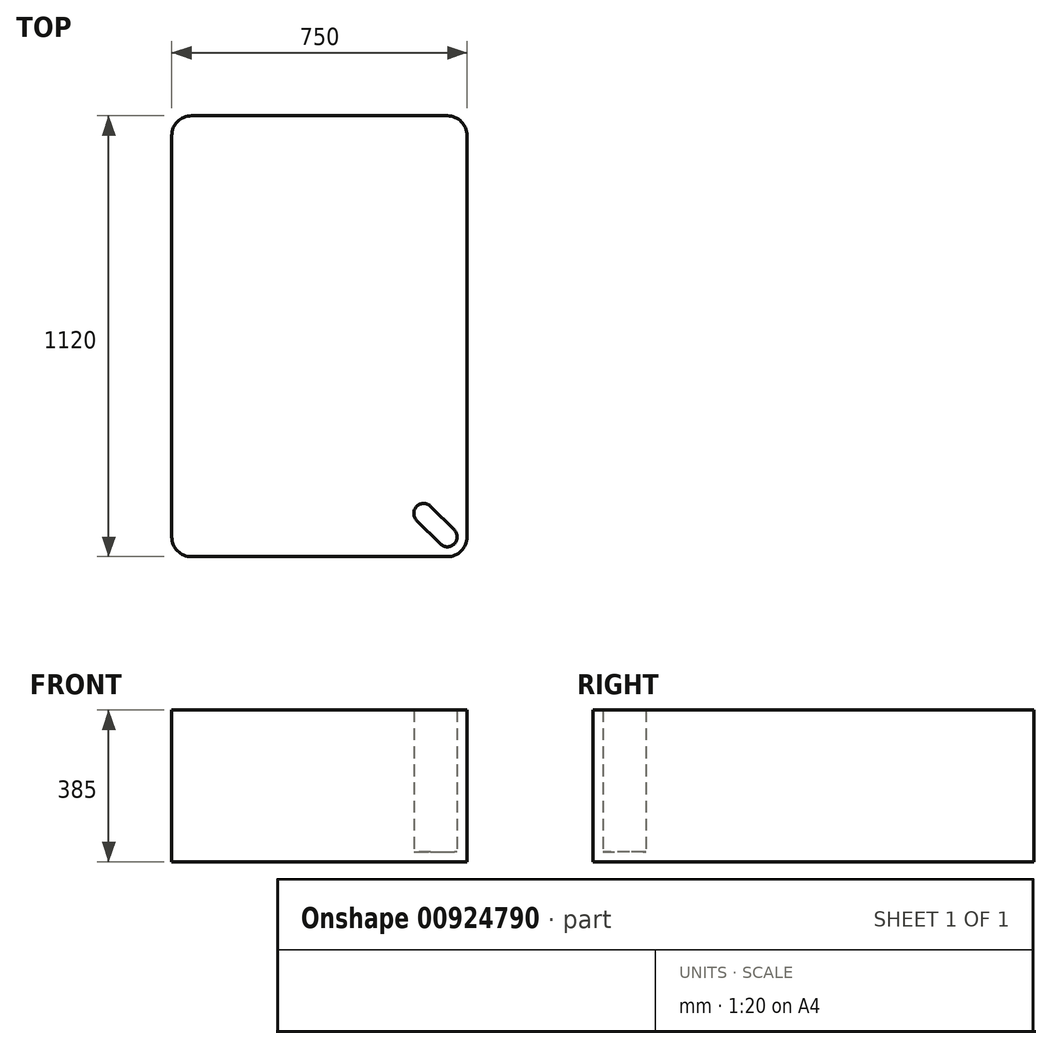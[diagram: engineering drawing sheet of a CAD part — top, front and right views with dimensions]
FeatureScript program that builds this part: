
annotation { "Feature Type Name" : "Feature", "Feature Type Description" : "" }
export const myFeature = defineFeature(function(context is Context, id is Id, definition is map)
    precondition{}
    {
        {
            var Q0;
            Q0=qCreatedBy(makeId("Top.planeOp"),FACE);
            var sketch = newSketch(context, id + "F0", { "sketchPlane" : qUnion([Q0])});
            skLineSegment(sketch, "E0.bottom", {"start": v(-325, 560) * mm, "end": v(325, 560) * mm});
            skLineSegment(sketch, "E0.top", {"start": v(-325, -560) * mm, "end": v(325, -560) * mm});
            skLineSegment(sketch, "E0.left", {"start": v(-375, 510) * mm, "end": v(-375, -510) * mm});
            skLineSegment(sketch, "E0.right", {"start": v(375, 510) * mm, "end": v(375, -510) * mm});
            skPoint(sketch, "E1.visualSharp", {"position": v(-375, 560) * mm});
            skArc(sketch, "E1.filletArc", {"start": v(-325, 560) * mm, "mid": v(-360.36, 545.36) * mm, "end": v(-375, 510) * mm});
            skPoint(sketch, "E2.visualSharp", {"position": v(375, 560) * mm});
            skArc(sketch, "E2.filletArc", {"start": v(375, 510) * mm, "mid": v(360.36, 545.36) * mm, "end": v(325, 560) * mm});
            skPoint(sketch, "E3.visualSharp", {"position": v(375, -560) * mm});
            skArc(sketch, "E3.filletArc", {"start": v(325, -560) * mm, "mid": v(360.36, -545.36) * mm, "end": v(375, -510) * mm});
            skPoint(sketch, "E4.visualSharp", {"position": v(-375, -560) * mm});
            skArc(sketch, "E4.filletArc", {"start": v(-375, -510) * mm, "mid": v(-360.36, -545.36) * mm, "end": v(-325, -560) * mm});
            skSolve(sketch);
        }
        {
            var Q0;
            Q0=makeQuery(id+"F0.imprint","IMPRINT",FACE,{"disambiguationData":[TD([[makeQuery(id+"F0.imprint","IMPRINT",EDGE,{"derivedFrom":sQuery(id+"F0.wireOp",EDGE,"E0.bottom")}),-1.0]])]});
            extrude(context, id + "F1", {"entities" : qUnion([Q0]), "depth" : 25 * mm, "offsetDistance" : 25 * mm});
        }
        {
            var Q0;
            Q0=makeQuery(id+"F1.opExtrude","CAP_FACE",FACE,{"disambiguationData":[OSD([sQuery(id+"F0.wireOp",EDGE,"E0.bottom"),sQuery(id+"F0.wireOp",EDGE,"E0.top"),sQuery(id+"F0.wireOp",EDGE,"E0.left"),sQuery(id+"F0.wireOp",EDGE,"E0.right"),sQuery(id+"F0.wireOp",EDGE,"E1.filletArc"),sQuery(id+"F0.wireOp",EDGE,"E2.filletArc"),sQuery(id+"F0.wireOp",EDGE,"E3.filletArc"),sQuery(id+"F0.wireOp",EDGE,"E4.filletArc")])],"isStart":false});
            var sketch = newSketch(context, id + "F2", { "sketchPlane" : qUnion([Q0])});
            skArc(sketch, "E5", {"start": v(-342.68, -492.32) * mm, "mid": v(-342.68, -527.68) * mm, "end": v(-307.32, -527.68) * mm});
            skArc(sketch, "E6", {"start": v(-247.32, -467.68) * mm, "mid": v(-247.32, -432.32) * mm, "end": v(-282.68, -432.32) * mm});
            skLineSegment(sketch, "E7", {"start": v(-282.68, -432.32) * mm, "end": v(-342.68, -492.32) * mm});
            skLineSegment(sketch, "E8", {"start": v(-247.32, -467.68) * mm, "end": v(-307.32, -527.68) * mm});
            skLineSegment(sketch, "E9.MirrorCS", {"start": v(282.68, -432.32) * mm, "end": v(342.68, -492.32) * mm});
            skArc(sketch, "E10.MirrorCS", {"start": v(342.68, -492.32) * mm, "mid": v(342.68, -527.68) * mm, "end": v(307.32, -527.68) * mm});
            skArc(sketch, "E11.MirrorCS", {"start": v(247.32, -467.68) * mm, "mid": v(247.32, -432.32) * mm, "end": v(282.68, -432.32) * mm});
            skLineSegment(sketch, "E12.MirrorCS", {"start": v(247.32, -467.68) * mm, "end": v(307.32, -527.68) * mm});
            skArc(sketch, "E13.MirrorCS", {"start": v(342.68, 492.32) * mm, "mid": v(342.68, 527.68) * mm, "end": v(307.32, 527.68) * mm});
            skLineSegment(sketch, "E14.MirrorCS", {"start": v(282.68, 432.32) * mm, "end": v(342.68, 492.32) * mm});
            skArc(sketch, "E15.MirrorCS", {"start": v(247.32, 467.68) * mm, "mid": v(247.32, 432.32) * mm, "end": v(282.68, 432.32) * mm});
            skLineSegment(sketch, "E16.MirrorCS", {"start": v(-247.32, 467.68) * mm, "end": v(-307.32, 527.68) * mm});
            skLineSegment(sketch, "E17.MirrorCS", {"start": v(247.32, 467.68) * mm, "end": v(307.32, 527.68) * mm});
            skArc(sketch, "E18.MirrorCS", {"start": v(-247.32, 467.68) * mm, "mid": v(-247.32, 432.32) * mm, "end": v(-282.68, 432.32) * mm});
            skLineSegment(sketch, "E19.MirrorCS", {"start": v(-282.68, 432.32) * mm, "end": v(-342.68, 492.32) * mm});
            skArc(sketch, "E20.MirrorCS", {"start": v(-342.68, 492.32) * mm, "mid": v(-342.68, 527.68) * mm, "end": v(-307.32, 527.68) * mm});
            skSolve(sketch);
        }
        {
            var Q0;
            Q0=makeQuery(id+"F2.imprint","IMPRINT",FACE,{"disambiguationData":[TD([[makeQuery(id+"F2.imprint","IMPRINT",EDGE,{"derivedFrom":sQuery(id+"F2.wireOp",EDGE,"E5")}),1.0]])]});
            var Q1;
            Q1=makeQuery(id+"F2.imprint","IMPRINT",FACE,{"disambiguationData":[TD([[makeQuery(id+"F2.imprint","IMPRINT",EDGE,{"derivedFrom":sQuery(id+"F2.wireOp",EDGE,"E10.MirrorCS")}),-1.0]])]});
            var Q2;
            Q2=makeQuery(id+"F2.imprint","IMPRINT",FACE,{"disambiguationData":[TD([[makeQuery(id+"F2.imprint","IMPRINT",EDGE,{"derivedFrom":sQuery(id+"F2.wireOp",EDGE,"E13.MirrorCS")}),1.0]])]});
            var Q3;
            Q3=makeQuery(id+"F2.imprint","IMPRINT",FACE,{"disambiguationData":[TD([[makeQuery(id+"F2.imprint","IMPRINT",EDGE,{"derivedFrom":sQuery(id+"F2.wireOp",EDGE,"E16.MirrorCS")}),1.0]])]});
            extrude(context, id + "F3", {"entities" : qUnion([Q0, Q1, Q2, Q3]), "operationType" : NewBodyOperationType.ADD, "depth" : 360 * mm, "offsetDistance" : 25 * mm});
        }
    });
